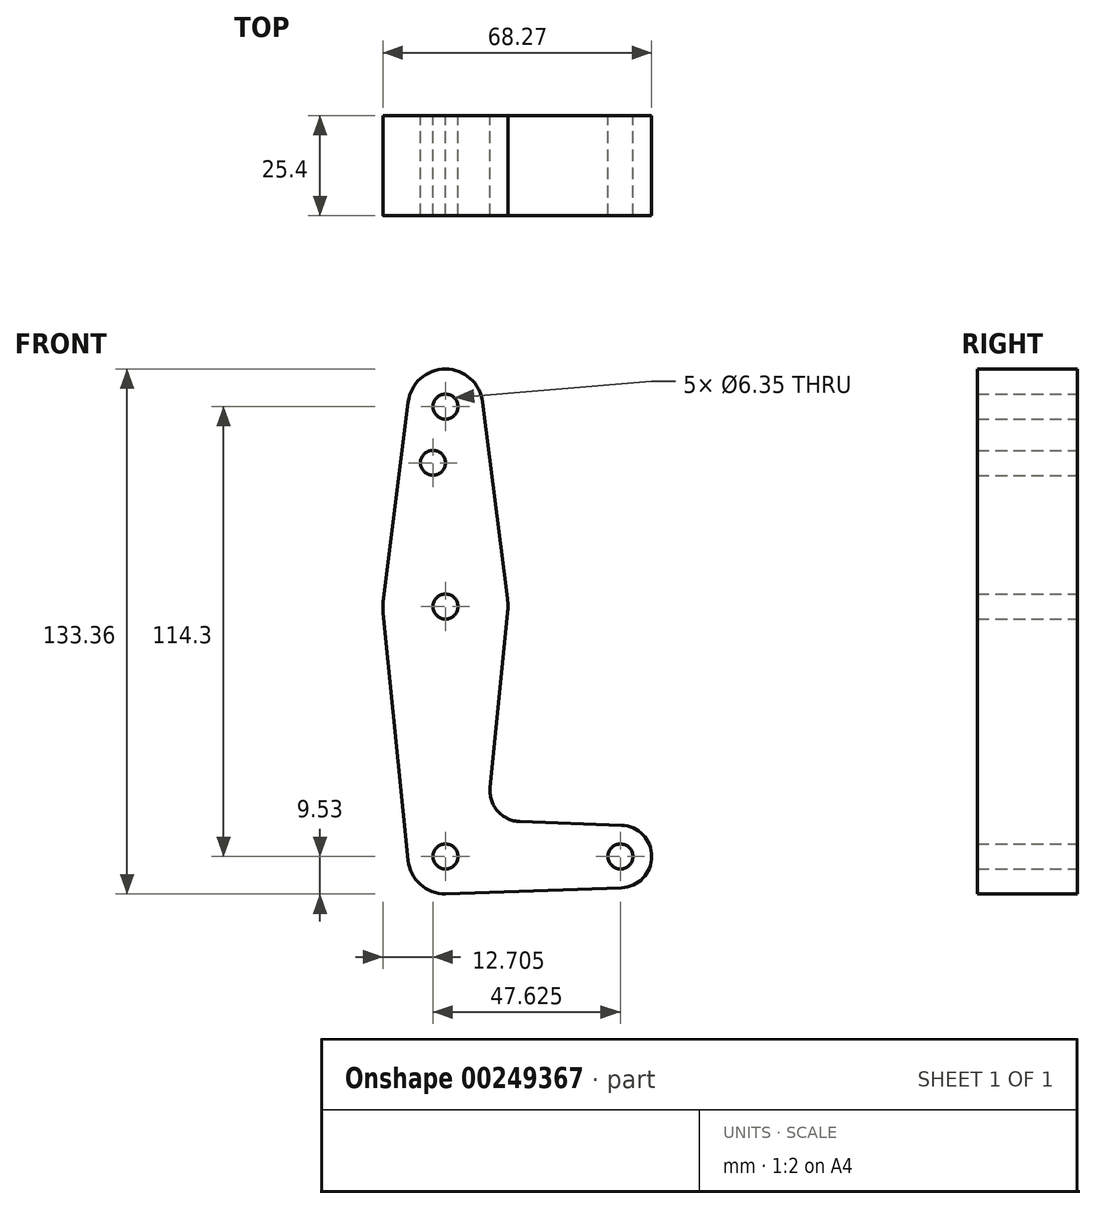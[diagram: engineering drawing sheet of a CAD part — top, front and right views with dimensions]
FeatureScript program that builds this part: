
annotation { "Feature Type Name" : "Feature", "Feature Type Description" : "" }
export const myFeature = defineFeature(function(context is Context, id is Id, definition is map)
    precondition{}
    {
        {
            var Q0;
            Q0=qCreatedBy(makeId("Front.planeOp"),FACE);
            var sketch = newSketch(context, id + "F0", { "sketchPlane" : qUnion([Q0])});
            skLineSegment(sketch, "E0", {"start": v(0, 0) * mm, "end": v(44.45, 0) * mm});
            skLineSegment(sketch, "E1", {"start": v(0, 0) * mm, "end": v(0, 114.3) * mm});
            skCircle(sketch, "E2", {"center": v(0, 0) * mm, "radius": 9.53 * mm});
            skCircle(sketch, "E3", {"center": v(44.45, 0) * mm, "radius": 7.94 * mm});
            skCircle(sketch, "E4", {"center": v(0, 114.3) * mm, "radius": 9.53 * mm});
            skCircle(sketch, "E5", {"center": v(0, 63.5) * mm, "radius": 15.88 * mm});
            skLineSegment(sketch, "E6", {"start": v(9.45, 115.5) * mm, "end": v(15.75, 65.48) * mm});
            skLineSegment(sketch, "E7", {"start": v(-9.45, 115.5) * mm, "end": v(-15.75, 65.48) * mm});
            skLineSegment(sketch, "E8", {"start": v(0, -9.53) * mm, "end": v(44.73, -7.93) * mm});
            skLineSegment(sketch, "E9", {"start": v(44.73, 7.93) * mm, "end": v(18.97, 8.85) * mm});
            skCircle(sketch, "E10", {"center": v(0, 114.3) * mm, "radius": 3.18 * mm});
            skCircle(sketch, "E11", {"center": v(0, 63.5) * mm, "radius": 3.18 * mm});
            skCircle(sketch, "E12", {"center": v(0, 0) * mm, "radius": 3.18 * mm});
            skCircle(sketch, "E13", {"center": v(44.45, 0) * mm, "radius": 3.18 * mm});
            skCircle(sketch, "E14", {"center": v(-3.18, 100.03) * mm, "radius": 3.18 * mm});
            skArc(sketch, "E15.filletArc", {"start": v(11.34, 17.59) * mm, "mid": v(13.26, 11.57) * mm, "end": v(18.97, 8.85) * mm});
            skLineSegment(sketch, "E16", {"start": v(-9.48, -0.95) * mm, "end": v(-15.8, 61.91) * mm});
            skLineSegment(sketch, "E17", {"start": v(11.34, 17.59) * mm, "end": v(15.8, 61.91) * mm});
            skSolve(sketch);
        }
        {
            var Q0;
            Q0=makeQuery(id+"F0.imprint","IMPRINT",FACE,{"disambiguationData":[TD([[makeQuery(id+"F0.imprint","IMPRINT",EDGE,{"derivedFrom":sQuery(id+"F0.wireOp",EDGE,"E10")}),-1.0]])]});
            var Q1;
            {var subQ0=sQuery(id+"F0.wireOp",EDGE,"E6");Q1=makeQuery(id+"F0.imprint","IMPRINT",FACE,{"disambiguationData":[TD([[makeQuery(id+"F0.imprint","IMPRINT",EDGE,{"derivedFrom":subQ0}),-1.0]])]});}
            var Q2;
            {var subQ0=sQuery(id+"F0.wireOp",EDGE,"E7");Q2=makeQuery(id+"F0.imprint","IMPRINT",FACE,{"disambiguationData":[TD([[makeQuery(id+"F0.imprint","IMPRINT",EDGE,{"derivedFrom":subQ0}),1.0]])]});}
            var Q3;
            {var subQ0=sQuery(id+"F0.wireOp",EDGE,"E5");var subQ2=sQuery(id+"F0.wireOp",EDGE,"E1");var subQ5=makeQuery(id+"F0.imprint","INTERSECT",VERTEX,{"disambiguationData":[OD(0.0)],"derivedFrom":[subQ2,subQ0]});Q3=makeQuery(id+"F0.imprint","IMPRINT",FACE,{"disambiguationData":[TD([[makeQuery(id+"F0.imprint","IMPRINT",EDGE,{"disambiguationData":[TD([[subQ5,-1.0]])],"derivedFrom":subQ2}),1.0]])]});}
            var Q4;
            {var subQ0=sQuery(id+"F0.wireOp",EDGE,"E5");var subQ2=sQuery(id+"F0.wireOp",EDGE,"E1");var subQ3=makeQuery(id+"F0.imprint","INTERSECT",VERTEX,{"disambiguationData":[OD(0.0)],"derivedFrom":[subQ2,subQ0]});Q4=makeQuery(id+"F0.imprint","IMPRINT",FACE,{"disambiguationData":[TD([[makeQuery(id+"F0.imprint","IMPRINT",EDGE,{"disambiguationData":[TD([[subQ3,-1.0]])],"derivedFrom":subQ2}),-1.0]])]});}
            var Q5;
            {var subQ7=sQuery(id+"F0.wireOp",EDGE,"E9");Q5=makeQuery(id+"F0.imprint","IMPRINT",FACE,{"disambiguationData":[TD([[makeQuery(id+"F0.imprint","IMPRINT",EDGE,{"derivedFrom":subQ7}),1.0]])]});}
            var Q6;
            {var subQ5=sQuery(id+"F0.wireOp",EDGE,"E16");Q6=makeQuery(id+"F0.imprint","IMPRINT",FACE,{"disambiguationData":[TD([[makeQuery(id+"F0.imprint","IMPRINT",EDGE,{"derivedFrom":subQ5}),-1.0]])]});}
            var Q7;
            {var subQ4=sQuery(id+"F0.wireOp",EDGE,"E12");var subQ5=sQuery(id+"F0.wireOp",EDGE,"E0");var subQ6=makeQuery(id+"F0.imprint","INTERSECT",VERTEX,{"derivedFrom":[subQ5,subQ4]});Q7=makeQuery(id+"F0.imprint","IMPRINT",FACE,{"disambiguationData":[TD([[makeQuery(id+"F0.imprint","IMPRINT",EDGE,{"disambiguationData":[TD([[subQ6,-1.0]])],"derivedFrom":subQ5}),-1.0]])]});}
            var Q8;
            {var subQ0=sQuery(id+"F0.wireOp",EDGE,"E12");var subQ1=sQuery(id+"F0.wireOp",EDGE,"E0");var subQ2=makeQuery(id+"F0.imprint","INTERSECT",VERTEX,{"derivedFrom":[subQ1,subQ0]});Q8=makeQuery(id+"F0.imprint","IMPRINT",FACE,{"disambiguationData":[TD([[makeQuery(id+"F0.imprint","IMPRINT",EDGE,{"disambiguationData":[TD([[subQ2,-1.0]])],"derivedFrom":subQ1}),1.0]])]});}
            var Q9;
            {var subQ0=sQuery(id+"F0.wireOp",EDGE,"E3");var subQ1=sQuery(id+"F0.wireOp",EDGE,"E0");var subQ2=makeQuery(id+"F0.imprint","INTERSECT",VERTEX,{"derivedFrom":[subQ1,subQ0]});Q9=makeQuery(id+"F0.imprint","IMPRINT",FACE,{"disambiguationData":[TD([[makeQuery(id+"F0.imprint","IMPRINT",EDGE,{"disambiguationData":[TD([[subQ2,1.0]])],"derivedFrom":subQ1}),-1.0]])]});}
            var Q10;
            Q10=makeQuery(id+"F0.imprint","IMPRINT",FACE,{"disambiguationData":[TD([[makeQuery(id+"F0.imprint","IMPRINT",EDGE,{"derivedFrom":sQuery(id+"F0.wireOp",EDGE,"E13")}),-1.0]])]});
            extrude(context, id + "F1", {"entities" : qUnion([Q0, Q1, Q2, Q3, Q4, Q5, Q6, Q7, Q8, Q9, Q10]), "depth" : 25.4 * mm});
        }
    });
